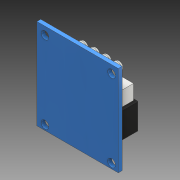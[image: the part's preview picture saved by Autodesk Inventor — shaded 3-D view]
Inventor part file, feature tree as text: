
AUTODESK INVENTOR PART (.ipt)
format: ipt  version: 2017 (Build 210142000, 142)  size: 157,184 bytes
history: native  units: mm
features: extrude x4, sketch x2, fillet x1
ambient origin geometry x8: Origin, YZ Plane, XZ Plane, XY Plane, X Axis, Y Axis, Z Axis, Center Point
bodies: Solid1 (feature_tree)
feature tree (7):
  extrude  "Extrusion1"  Depth=35.0mm
  sketch  "Sketch2"  dims[d2=3.0mm d3=25.8mm d4=2.6mm d5=30.0mm d6=2.0mm d7=1.5mm d8=0.0mm d9=10.0mm d10=20.4mm d11=8.24mm d12=2.0mm d13=8.11mm d14=0.0mm d15=15.0mm d16=5.71mm d17=2.5mm d18=10.45mm d19=0.75mm d20=6.9mm d21=0.0mm d22=4.5mm d23=4.5mm d24=4.5mm d25=6.5mm d26=5.6mm d27=3.5mm d28=5.6mm d29=0.0mm d30=1.0mm]
  extrude  "Extrusion2"  Depth=1.0mm
  extrude  "Extrusion3"  Depth=1.0mm
  extrude  "Extrusion4"  Depth=1.0mm
  fillet  "Fillet1"  Radius=2.0mm
  sketch  "Sketch1"  dims[d0=31.55mm d1=35.0mm]
